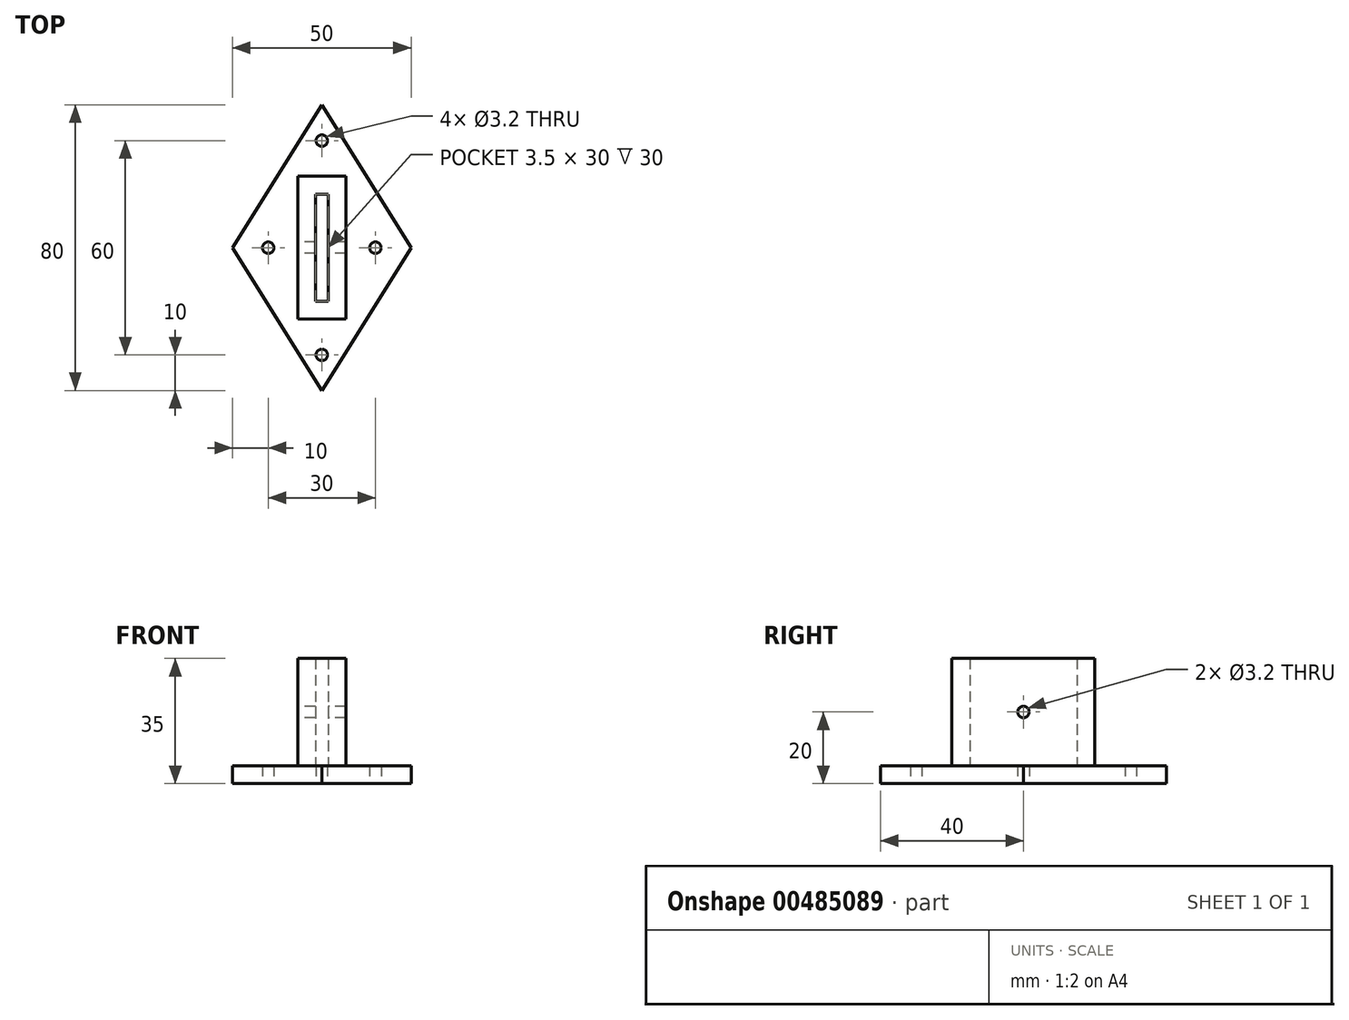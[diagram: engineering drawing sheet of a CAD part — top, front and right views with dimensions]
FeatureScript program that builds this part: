
annotation { "Feature Type Name" : "Feature", "Feature Type Description" : "" }
export const myFeature = defineFeature(function(context is Context, id is Id, definition is map)
    precondition{}
    {
        {
            var Q0;
            Q0=qCreatedBy(makeId("Top.planeOp"),FACE);
            var sketch = newSketch(context, id + "F0", { "sketchPlane" : qUnion([Q0])});
            skLineSegment(sketch, "E0", {"start": v(-25, 0) * mm, "end": v(25, 0) * mm});
            skLineSegment(sketch, "E1", {"start": v(0, 40) * mm, "end": v(0, -40) * mm});
            skLineSegment(sketch, "E2", {"start": v(0, 40) * mm, "end": v(-25, 0) * mm});
            skLineSegment(sketch, "E3", {"start": v(0, 40) * mm, "end": v(25, 0) * mm});
            skLineSegment(sketch, "E4", {"start": v(-25, 0) * mm, "end": v(0, -40) * mm});
            skLineSegment(sketch, "E5", {"start": v(25, 0) * mm, "end": v(0, -40) * mm});
            skLineSegment(sketch, "E6", {"start": v(0, 30) * mm, "end": v(0, -30) * mm});
            skLineSegment(sketch, "E7", {"start": v(-15, 0) * mm, "end": v(15, 0) * mm});
            skCircle(sketch, "E8", {"center": v(-15, 0) * mm, "radius": 1.6 * mm});
            skCircle(sketch, "E9", {"center": v(15, 0) * mm, "radius": 1.6 * mm});
            skCircle(sketch, "E10", {"center": v(0, -30) * mm, "radius": 1.6 * mm});
            skCircle(sketch, "E11", {"center": v(0, 30) * mm, "radius": 1.6 * mm});
            skSolve(sketch);
        }
        {
            var Q0;
            Q0 = qSketchRegion(id + "F0", true);
            extrude(context, id + "F1", {"entities" : qUnion([Q0]), "depth" : 5 * mm});
        }
        {
            var Q0;
            Q0=makeQuery(id+"F1.opExtrude","CAP_FACE",FACE,{"disambiguationData":[OSD([sQuery(id+"F0.wireOp",EDGE,"E2"),sQuery(id+"F0.wireOp",EDGE,"E3"),sQuery(id+"F0.wireOp",EDGE,"E4"),sQuery(id+"F0.wireOp",EDGE,"E5"),sQuery(id+"F0.wireOp",EDGE,"E8"),sQuery(id+"F0.wireOp",EDGE,"E9"),sQuery(id+"F0.wireOp",EDGE,"E10"),sQuery(id+"F0.wireOp",EDGE,"E11")])],"isStart":false});
            var sketch = newSketch(context, id + "F2", { "sketchPlane" : qUnion([Q0])});
            skLineSegment(sketch, "E12", {"start": v(0, 20) * mm, "end": v(0, -20) * mm});
            skLineSegment(sketch, "E13", {"start": v(-6.75, 0) * mm, "end": v(6.75, 0) * mm});
            skLineSegment(sketch, "E14.bottom", {"start": v(6.75, -20) * mm, "end": v(-6.75, -20) * mm});
            skLineSegment(sketch, "E14.top", {"start": v(6.75, 20) * mm, "end": v(-6.75, 20) * mm});
            skLineSegment(sketch, "E14.left", {"start": v(6.75, -20) * mm, "end": v(6.75, 20) * mm});
            skLineSegment(sketch, "E14.right", {"start": v(-6.75, -20) * mm, "end": v(-6.75, 20) * mm});
            skPoint(sketch, "E14.middle", {"position": v(0, 0) * mm});
            skLineSegment(sketch, "E15", {"start": v(-1.75, 0) * mm, "end": v(1.75, 0) * mm});
            skLineSegment(sketch, "E16", {"start": v(0, 15) * mm, "end": v(0, -15) * mm});
            skLineSegment(sketch, "E17.bottom", {"start": v(1.75, -15) * mm, "end": v(-1.75, -15) * mm});
            skLineSegment(sketch, "E17.top", {"start": v(1.75, 15) * mm, "end": v(-1.75, 15) * mm});
            skLineSegment(sketch, "E17.left", {"start": v(1.75, -15) * mm, "end": v(1.75, 15) * mm});
            skLineSegment(sketch, "E17.right", {"start": v(-1.75, -15) * mm, "end": v(-1.75, 15) * mm});
            skSolve(sketch);
        }
        {
            var Q0;
            {var subQ3=sQuery(id+"F2.wireOp",EDGE,"E14.top");var subQ5=sQuery(id+"F2.wireOp",EDGE,"E12");var subQ6=makeQuery(id+"F2.imprint","INTERSECT",VERTEX,{"derivedFrom":[subQ5,subQ3]});Q0=makeQuery(id+"F2.imprint","IMPRINT",FACE,{"disambiguationData":[TD([[makeQuery(id+"F2.imprint","IMPRINT",EDGE,{"disambiguationData":[TD([[subQ6,-1.0]])],"derivedFrom":subQ3}),1.0]])]});}
            var Q1;
            {var subQ3=sQuery(id+"F2.wireOp",EDGE,"E14.top");var subQ5=sQuery(id+"F2.wireOp",EDGE,"E12");var subQ6=makeQuery(id+"F2.imprint","INTERSECT",VERTEX,{"derivedFrom":[subQ5,subQ3]});Q1=makeQuery(id+"F2.imprint","IMPRINT",FACE,{"disambiguationData":[TD([[makeQuery(id+"F2.imprint","IMPRINT",EDGE,{"disambiguationData":[TD([[subQ6,1.0]])],"derivedFrom":subQ3}),1.0]])]});}
            var Q2;
            {var subQ3=sQuery(id+"F2.wireOp",EDGE,"E14.bottom");var subQ5=sQuery(id+"F2.wireOp",EDGE,"E12");var subQ6=makeQuery(id+"F2.imprint","INTERSECT",VERTEX,{"derivedFrom":[subQ5,subQ3]});Q2=makeQuery(id+"F2.imprint","IMPRINT",FACE,{"disambiguationData":[TD([[makeQuery(id+"F2.imprint","IMPRINT",EDGE,{"disambiguationData":[TD([[subQ6,-1.0]])],"derivedFrom":subQ3}),-1.0]])]});}
            var Q3;
            {var subQ0=sQuery(id+"F2.wireOp",EDGE,"E14.bottom");var subQ1=sQuery(id+"F2.wireOp",EDGE,"E12");var subQ2=makeQuery(id+"F2.imprint","INTERSECT",VERTEX,{"derivedFrom":[subQ1,subQ0]});Q3=makeQuery(id+"F2.imprint","IMPRINT",FACE,{"disambiguationData":[TD([[makeQuery(id+"F2.imprint","IMPRINT",EDGE,{"disambiguationData":[TD([[subQ2,1.0]])],"derivedFrom":subQ0}),-1.0]])]});}
            extrude(context, id + "F3", {"entities" : qUnion([Q0, Q1, Q2, Q3]), "operationType" : NewBodyOperationType.ADD, "depth" : 30 * mm});
        }
        {
            var Q0;
            Q0=makeQuery(id+"F3.opExtrude","SWEPT_FACE",FACE,{"disambiguationData":[OSD([sQuery(id+"F2.wireOp",EDGE,"E14.right")])]});
            var sketch = newSketch(context, id + "F4", { "sketchPlane" : qUnion([Q0])});
            skLineSegment(sketch, "E18.bottom", {"start": v(-20, 5) * mm, "end": v(0, 5) * mm});
            skLineSegment(sketch, "E18.top", {"start": v(-20, 20) * mm, "end": v(0, 20) * mm});
            skLineSegment(sketch, "E18.left", {"start": v(-20, 5) * mm, "end": v(-20, 20) * mm});
            skLineSegment(sketch, "E18.right", {"start": v(0, 5) * mm, "end": v(0, 20) * mm});
            skCircle(sketch, "E19", {"center": v(0, 20) * mm, "radius": 1.6 * mm});
            skSolve(sketch);
        }
        {
            var Q0;
            {var subQ0=sQuery(id+"F4.wireOp",EDGE,"E18.right");var subQ1=sQuery(id+"F4.wireOp",EDGE,"E18.top");var subQ2=makeQuery(id+"F4.imprint","INTERSECT",VERTEX,{"derivedFrom":[subQ1,subQ0]});Q0=makeQuery(id+"F4.imprint","IMPRINT",FACE,{"disambiguationData":[TD([[makeQuery(id+"F4.imprint","IMPRINT",EDGE,{"disambiguationData":[TD([[subQ2,1.0]])],"derivedFrom":subQ1}),-1.0]])]});}
            var Q1;
            {var subQ0=sQuery(id+"F4.wireOp",EDGE,"E18.right");var subQ1=sQuery(id+"F4.wireOp",EDGE,"E18.top");var subQ2=makeQuery(id+"F4.imprint","INTERSECT",VERTEX,{"derivedFrom":[subQ1,subQ0]});Q1=makeQuery(id+"F4.imprint","IMPRINT",FACE,{"disambiguationData":[TD([[makeQuery(id+"F4.imprint","IMPRINT",EDGE,{"disambiguationData":[TD([[subQ2,1.0]])],"derivedFrom":subQ1}),1.0]])]});}
            extrude(context, id + "F5", {"entities" : qUnion([Q0, Q1]), "operationType" : NewBodyOperationType.REMOVE, "endBound" : BoundingType.THROUGH_ALL, "oppositeDirection" : true, "depth" : 25 * mm});
        }
    });
